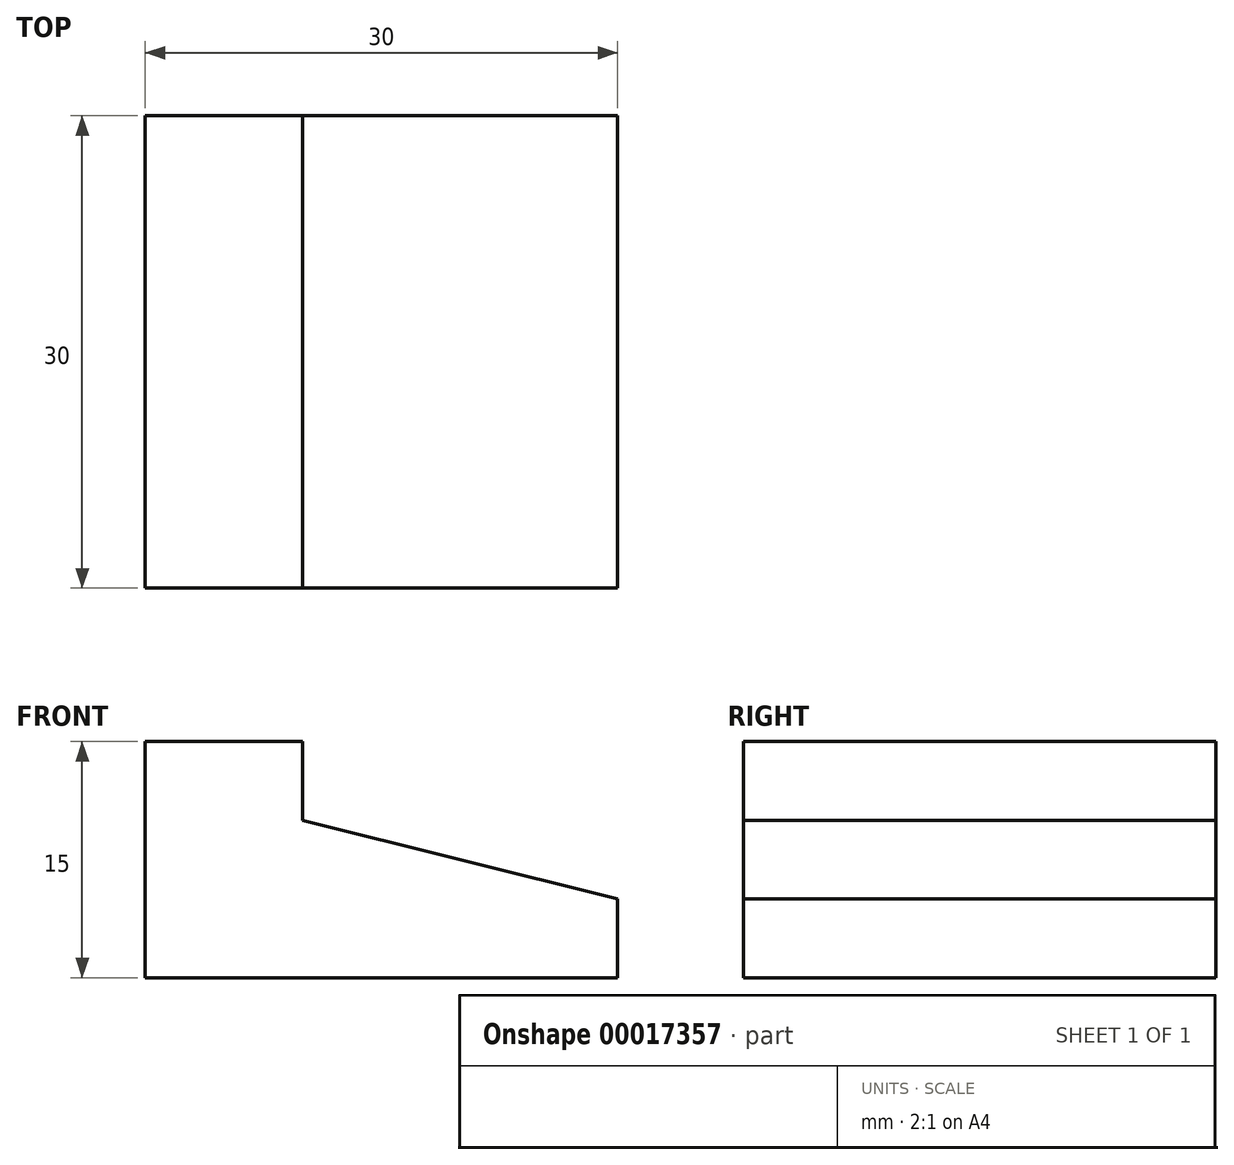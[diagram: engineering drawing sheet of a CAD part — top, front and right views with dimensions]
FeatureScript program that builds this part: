
annotation { "Feature Type Name" : "Feature", "Feature Type Description" : "" }
export const myFeature = defineFeature(function(context is Context, id is Id, definition is map)
    precondition{}
    {
        {
            var Q0;
            Q0=qCreatedBy(makeId("Front.planeOp"),FACE);
            var sketch = newSketch(context, id + "F0", { "sketchPlane" : qUnion([Q0])});
            skLineSegment(sketch, "E0", {"start": v(-11.4, 10.95) * mm, "end": v(-11.4, -4.05) * mm});
            skLineSegment(sketch, "E1", {"start": v(-11.4, -4.05) * mm, "end": v(18.6, -4.05) * mm});
            skLineSegment(sketch, "E2", {"start": v(18.6, -4.05) * mm, "end": v(18.6, 0.95) * mm});
            skLineSegment(sketch, "E3", {"start": v(18.6, 0.95) * mm, "end": v(-1.4, 5.95) * mm});
            skLineSegment(sketch, "E4", {"start": v(-1.4, 5.95) * mm, "end": v(-1.4, 10.95) * mm});
            skLineSegment(sketch, "E5", {"start": v(-1.4, 10.95) * mm, "end": v(-11.4, 10.95) * mm});
            skSolve(sketch);
        }
        {
            var Q0;
            Q0=makeQuery(id+"F0.imprint","IMPRINT",FACE,{"disambiguationData":[TD([[makeQuery(id+"F0.imprint","IMPRINT",EDGE,{"derivedFrom":sQuery(id+"F0.wireOp",EDGE,"E0")}),1.0]])]});
            extrude(context, id + "F1", {"entities" : qUnion([Q0]), "depth" : 30 * mm});
        }
    });
